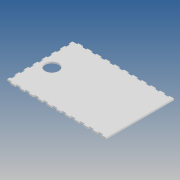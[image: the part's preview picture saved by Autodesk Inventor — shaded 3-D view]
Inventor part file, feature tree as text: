
AUTODESK INVENTOR PART (.ipt)
format: ipt  version: 2020 (Build 240168000, 168)  size: 196,608 bytes
history: native  units: mm
features: extrude x4, sketch x4, pattern_linear x2, mirror x1
ambient origin geometry x8: Origin, YZ Plane, XZ Plane, XY Plane, X Axis, Y Axis, Z Axis, Center Point
bodies: Body1 (feature_tree)
feature tree (11):
  extrude  "Выдавливание5"  Depth=220.0mm
  extrude  "Выдавливание6"  Depth=149.0mm
  pattern_linear  "Прямоуг.массив6"  Spacing1=3.0mm  [1 undecoded]
  extrude  "Выдавливание8"  Depth=3.0mm
  pattern_linear  "Прямоуг.массив7"  Spacing1=10.0mm  [1 undecoded]
  mirror  "Зеркальное отражение2"
  extrude  "Выдавливание9"  Depth=3.0mm TaperAngle=0.0deg
  sketch  "Эскиз5"
  sketch  "Эскиз6"
  sketch  "Эскиз8"
  sketch  "Эскиз9"
note: 2 required parameter values undecoded (feature->parameter linkage not recoverable at this tier; creation-order binding heuristic only, values carry confidence <= 0.55)
